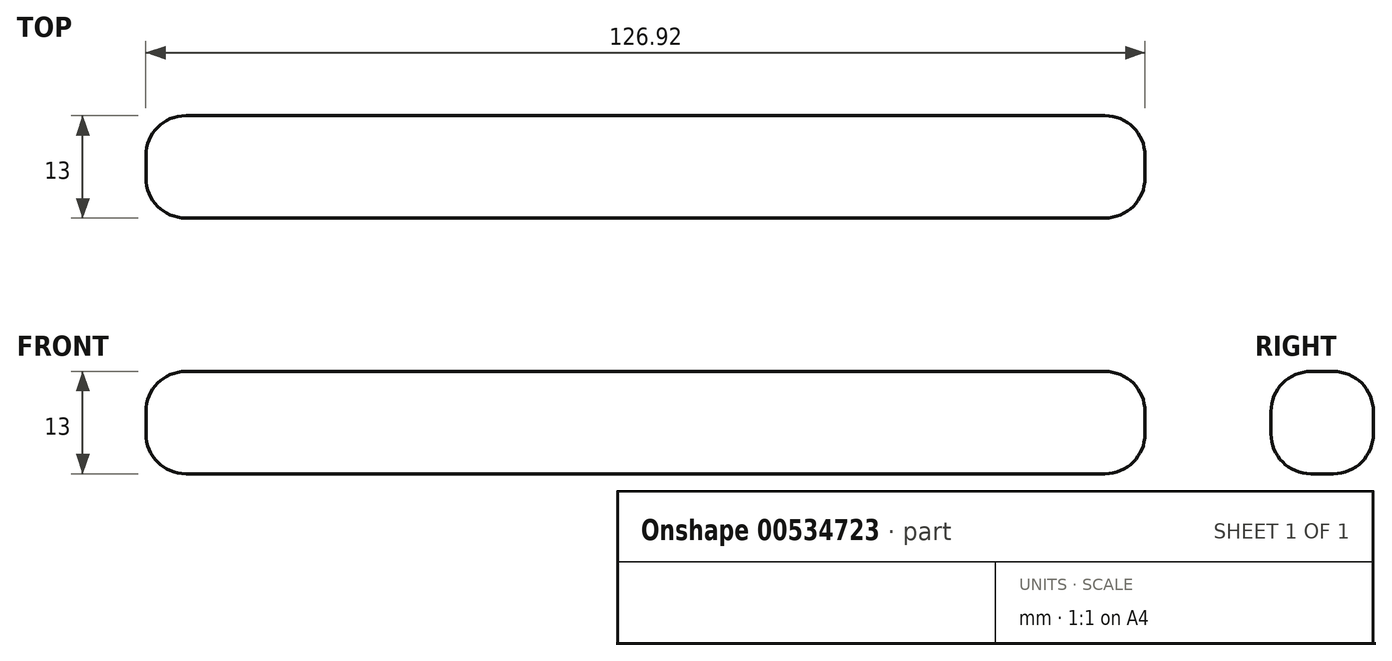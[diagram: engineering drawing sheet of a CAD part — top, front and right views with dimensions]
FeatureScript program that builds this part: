
annotation { "Feature Type Name" : "Feature", "Feature Type Description" : "" }
export const myFeature = defineFeature(function(context is Context, id is Id, definition is map)
    precondition{}
    {
        {
            var Q0;
            Q0=qCreatedBy(makeId("Top.planeOp"),FACE);
            var sketch = newSketch(context, id + "F0", { "sketchPlane" : qUnion([Q0])});
            skLineSegment(sketch, "E0.bottom", {"start": v(-63.46, -6.5) * mm, "end": v(63.46, -6.5) * mm});
            skLineSegment(sketch, "E0.top", {"start": v(-63.46, 6.5) * mm, "end": v(63.46, 6.5) * mm});
            skLineSegment(sketch, "E0.left", {"start": v(-63.46, -6.5) * mm, "end": v(-63.46, 6.5) * mm});
            skLineSegment(sketch, "E0.right", {"start": v(63.46, -6.5) * mm, "end": v(63.46, 6.5) * mm});
            skPoint(sketch, "E0.middle", {"position": v(0, 0) * mm});
            skSolve(sketch);
        }
        {
            var Q0;
            Q0=makeQuery(id+"F0.imprint","IMPRINT",FACE,{"disambiguationData":[TD([[makeQuery(id+"F0.imprint","IMPRINT",EDGE,{"derivedFrom":sQuery(id+"F0.wireOp",EDGE,"E0.bottom")}),1.0]])]});
            extrude(context, id + "F1", {"entities" : qUnion([Q0]), "depth" : 13 * mm, "offsetDistance" : 25.4 * mm});
        }
        {
            var Q0;
            Q0=makeQuery(id+"F1.opExtrude","CAP_FACE",FACE,{"disambiguationData":[OSD([sQuery(id+"F0.wireOp",EDGE,"E0.bottom"),sQuery(id+"F0.wireOp",EDGE,"E0.top"),sQuery(id+"F0.wireOp",EDGE,"E0.left"),sQuery(id+"F0.wireOp",EDGE,"E0.right")])],"isStart":false});
            var Q1;
            Q1=makeQuery(id+"F1.opExtrude","SWEPT_FACE",FACE,{"disambiguationData":[OSD([sQuery(id+"F0.wireOp",EDGE,"E0.bottom")])]});
            var Q2;
            Q2=makeQuery(id+"F1.opExtrude","SWEPT_FACE",FACE,{"disambiguationData":[OSD([sQuery(id+"F0.wireOp",EDGE,"E0.right")])]});
            var Q3;
            Q3=makeQuery(id+"F1.opExtrude","CAP_EDGE",EDGE,{"disambiguationData":[OSD([sQuery(id+"F0.wireOp",EDGE,"E0.right")])],"isStart":false});
            var Q4;
            Q4=makeQuery(id+"F1.opExtrude","CAP_EDGE",EDGE,{"disambiguationData":[OSD([sQuery(id+"F0.wireOp",EDGE,"E0.right")])],"isStart":true});
            var Q5;
            Q5=makeQuery(id+"F1.opExtrude","CAP_EDGE",EDGE,{"disambiguationData":[OSD([sQuery(id+"F0.wireOp",EDGE,"E0.top")])],"isStart":false});
            var Q6;
            Q6=makeQuery(id+"F1.opExtrude","CAP_EDGE",EDGE,{"disambiguationData":[OSD([sQuery(id+"F0.wireOp",EDGE,"E0.top")])],"isStart":true});
            var Q7;
            Q7=makeQuery(id+"F1.opExtrude","CAP_EDGE",EDGE,{"disambiguationData":[OSD([sQuery(id+"F0.wireOp",EDGE,"E0.bottom")])],"isStart":false});
            var Q8;
            Q8=makeQuery(id+"F1.opExtrude","SWEPT_EDGE",EDGE,{"disambiguationData":[OSD([sQuery(id+"F0.wireOp",EDGE,"E0.bottom"),sQuery(id+"F0.wireOp",EDGE,"E0.right")])]});
            var Q9;
            Q9=makeQuery(id+"F1.opExtrude","SWEPT_EDGE",EDGE,{"disambiguationData":[OSD([sQuery(id+"F0.wireOp",EDGE,"E0.top"),sQuery(id+"F0.wireOp",EDGE,"E0.left")])]});
            var Q10;
            Q10=makeQuery(id+"F1.opExtrude","SWEPT_EDGE",EDGE,{"disambiguationData":[OSD([sQuery(id+"F0.wireOp",EDGE,"E0.top"),sQuery(id+"F0.wireOp",EDGE,"E0.right")])]});
            var Q11;
            Q11=makeQuery(id+"F1.opExtrude","SWEPT_FACE",FACE,{"disambiguationData":[OSD([sQuery(id+"F0.wireOp",EDGE,"E0.top")])]});
            var Q12;
            Q12=makeQuery(id+"F1.opExtrude","CAP_EDGE",EDGE,{"disambiguationData":[OSD([sQuery(id+"F0.wireOp",EDGE,"E0.left")])],"isStart":false});
            var Q13;
            Q13=makeQuery(id+"F1.opExtrude","CAP_FACE",FACE,{"disambiguationData":[OSD([sQuery(id+"F0.wireOp",EDGE,"E0.bottom"),sQuery(id+"F0.wireOp",EDGE,"E0.top"),sQuery(id+"F0.wireOp",EDGE,"E0.left"),sQuery(id+"F0.wireOp",EDGE,"E0.right")])],"isStart":true});
            var Q14;
            Q14=makeQuery(id+"F1.opExtrude","SWEPT_FACE",FACE,{"disambiguationData":[OSD([sQuery(id+"F0.wireOp",EDGE,"E0.left")])]});
            fillet(context, id + "F2", {"entities" : qUnion([Q0, Q1, Q2, Q3, Q4, Q5, Q6, Q7, Q8, Q9, Q10, Q11, Q12, Q13, Q14]), "radius" : 5.08 * mm, "tangentPropagation" : true, "allowEdgeOverflow" : false});
        }
    });
